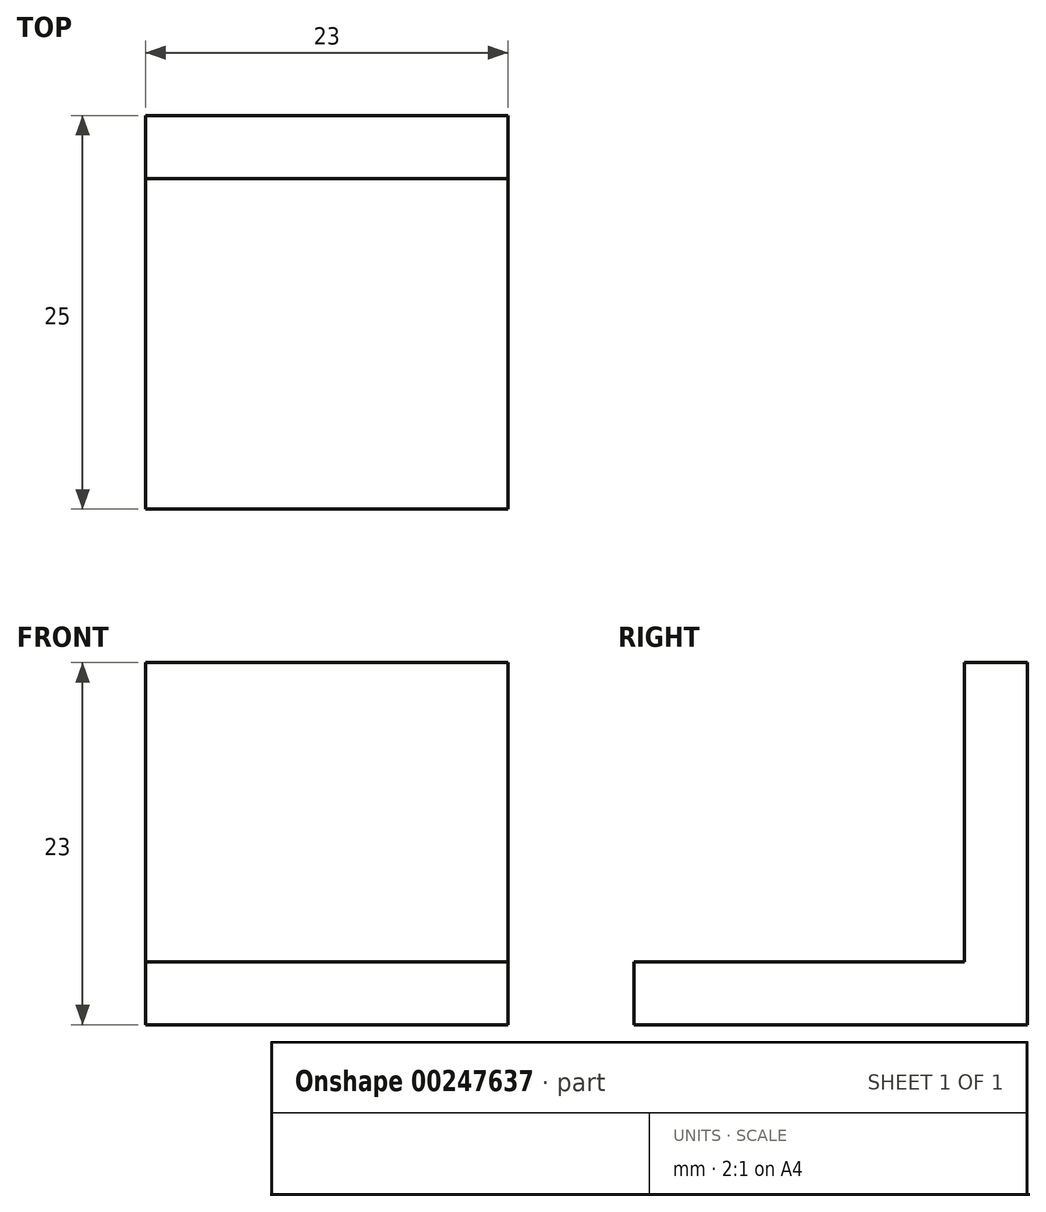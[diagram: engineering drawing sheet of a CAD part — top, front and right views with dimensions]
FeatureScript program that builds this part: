
annotation { "Feature Type Name" : "Feature", "Feature Type Description" : "" }
export const myFeature = defineFeature(function(context is Context, id is Id, definition is map)
    precondition{}
    {
        {
            var Q0;
            Q0=qCreatedBy(makeId("Front.planeOp"),FACE);
            var sketch = newSketch(context, id + "F0", { "sketchPlane" : qUnion([Q0])});
            skLineSegment(sketch, "E0.bottom", {"start": v(11.5, -11.5) * mm, "end": v(-11.5, -11.5) * mm});
            skLineSegment(sketch, "E0.top", {"start": v(11.5, 11.5) * mm, "end": v(-11.5, 11.5) * mm});
            skLineSegment(sketch, "E0.left", {"start": v(11.5, -11.5) * mm, "end": v(11.5, 11.5) * mm});
            skLineSegment(sketch, "E0.right", {"start": v(-11.5, -11.5) * mm, "end": v(-11.5, 11.5) * mm});
            skPoint(sketch, "E0.middle", {"position": v(0, 0) * mm});
            skLineSegment(sketch, "E1", {"start": v(-11.5, -7.5) * mm, "end": v(11.5, -7.5) * mm});
            skSolve(sketch);
        }
        {
            var Q0;
            Q0=makeQuery(id+"F0.imprint","IMPRINT",FACE,{"disambiguationData":[TD([[makeQuery(id+"F0.imprint","IMPRINT",EDGE,{"derivedFrom":sQuery(id+"F0.wireOp",EDGE,"E0.bottom")}),-1.0]])]});
            var Q1;
            {var subQ0=sQuery(id+"F0.wireOp",EDGE,"E0.top");Q1=makeQuery(id+"F0.imprint","IMPRINT",FACE,{"disambiguationData":[TD([[makeQuery(id+"F0.imprint","IMPRINT",EDGE,{"derivedFrom":subQ0}),1.0]])]});}
            extrude(context, id + "F1", {"entities" : qUnion([Q0, Q1]), "depth" : 4 * mm});
        }
        {
            var Q0;
            {var subQ0=sQuery(id+"F0.wireOp",EDGE,"E0.bottom");Q0=makeQuery(id+"F0.imprint","IMPRINT",FACE,{"disambiguationData":[TD([[makeQuery(id+"F0.imprint","IMPRINT",EDGE,{"derivedFrom":subQ0}),-1.0]])]});}
            extrude(context, id + "F2", {"entities" : qUnion([Q0]), "operationType" : NewBodyOperationType.ADD, "depth" : 25 * mm});
        }
    });
